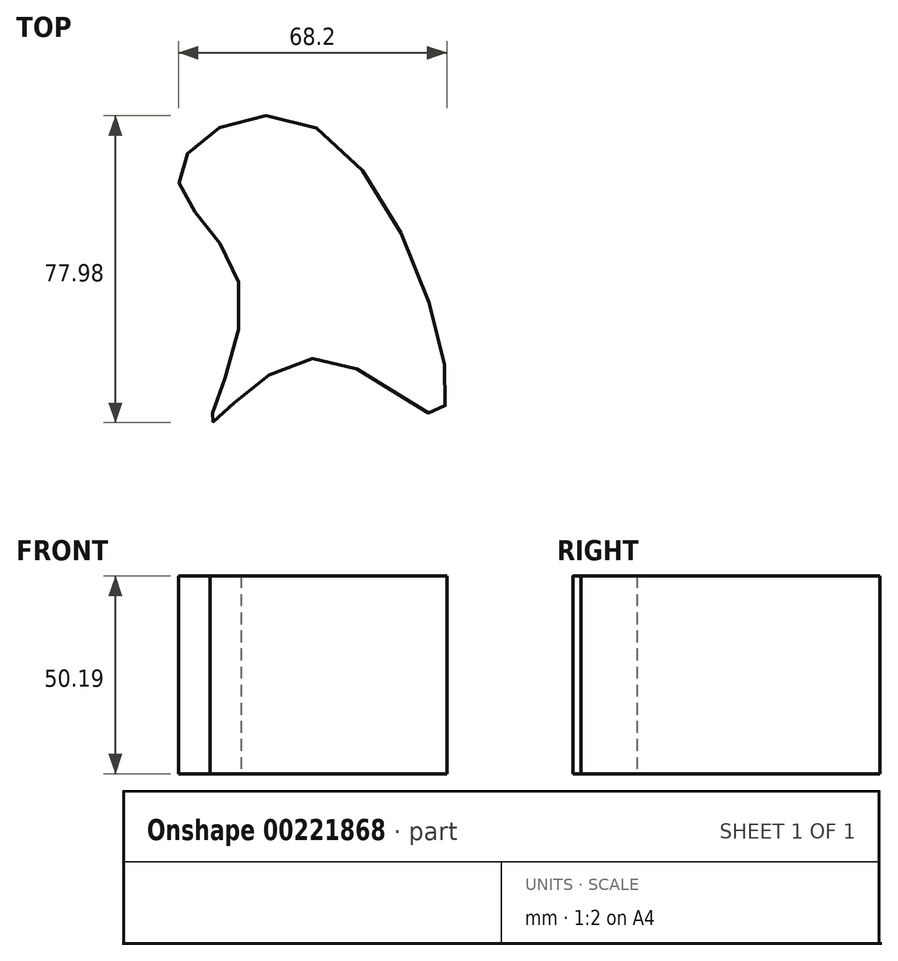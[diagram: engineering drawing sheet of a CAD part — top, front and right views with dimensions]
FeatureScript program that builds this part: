
annotation { "Feature Type Name" : "Feature", "Feature Type Description" : "" }
export const myFeature = defineFeature(function(context is Context, id is Id, definition is map)
    precondition{}
    {
        {
            var Q0;
            Q0=qCreatedBy(makeId("Top.planeOp"),FACE);
            var sketch = newSketch(context, id + "F0", { "sketchPlane" : qUnion([Q0])});
            skFitSpline(sketch, "E0", {"points": [v(0, 40.57) * mm, v(-35.01, 29.09) * mm, v(-19.45, 0) * mm, v(-26.86, -34.27) * mm, v(0, -17.97) * mm, v(31.68, -31.68) * mm, v(0, 40.57) * mm]});
            skSolve(sketch);
        }
        {
            var Q0;
            Q0 = qSketchRegion(id + "F0", true);
            extrude(context, id + "F1", {"entities" : qUnion([Q0]), "depth" : 50.2 * mm});
        }
    });
